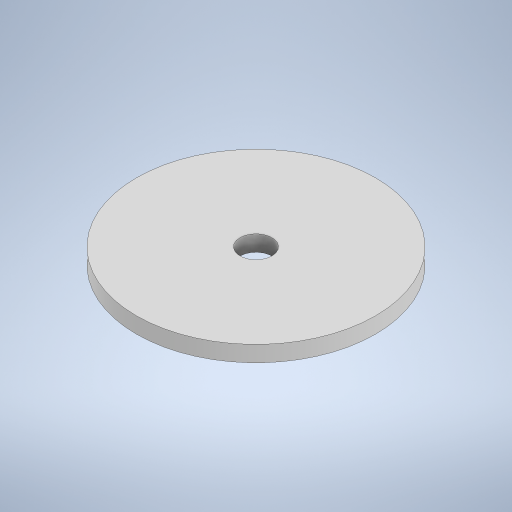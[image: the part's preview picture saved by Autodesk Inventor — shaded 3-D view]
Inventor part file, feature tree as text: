
AUTODESK INVENTOR PART (.ipt)
format: ipt  version: 2023 (Build 270158000, 158)  size: 210,432 bytes
history: native  units: mm
features: other x1, extrude x1, sketch x1
ambient origin geometry x8: Origin, YZ Plane, XZ Plane, XY Plane, X Axis, Y Axis, Z Axis, Center Point
bodies: Body1 (feature_tree)
feature tree (3):
  other  "Твердое тело1"
  extrude  "Выдавливание1"  Depth=4.0mm
  sketch  "Эскиз1"
